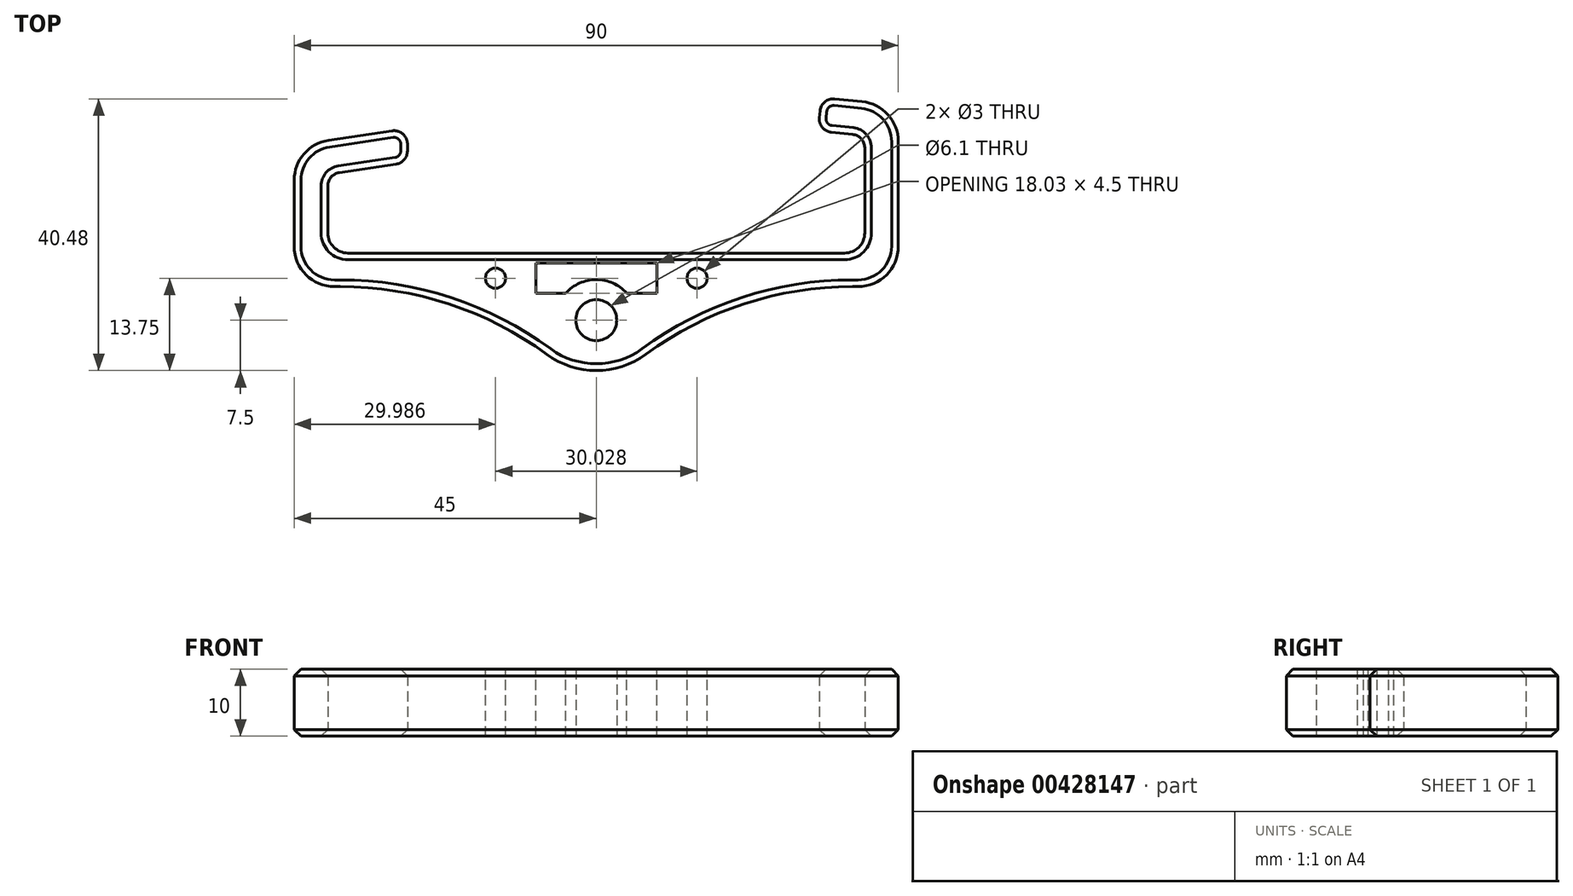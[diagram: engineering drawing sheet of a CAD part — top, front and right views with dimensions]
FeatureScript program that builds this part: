
annotation { "Feature Type Name" : "Feature", "Feature Type Description" : "" }
export const myFeature = defineFeature(function(context is Context, id is Id, definition is map)
    precondition{}
    {
        {
            var Q0;
            Q0=qCreatedBy(makeId("Right.planeOp"),FACE);
            var sketch = newSketch(context, id + "F0", { "sketchPlane" : qUnion([Q0])});
            skLineSegment(sketch, "E0", {"start": v(0, 77) * mm, "end": v(0, 3) * mm});
            skLineSegment(sketch, "E1", {"start": v(3, 80) * mm, "end": v(10, 80) * mm});
            skLineSegment(sketch, "E2", {"start": v(3, 0) * mm, "end": v(15.7, 0) * mm});
            skLineSegment(sketch, "E3", {"start": v(11.98, 78.3) * mm, "end": v(13.24, 69.84) * mm});
            skLineSegment(sketch, "E4", {"start": v(17.68, 1.8) * mm, "end": v(18, 4.97) * mm});
            skLineSegment(sketch, "E5.0", {"start": v(16.8, 79.89) * mm, "end": v(18.21, 70.43) * mm});
            skLineSegment(sketch, "E5.1", {"start": v(22.57, 0.4) * mm, "end": v(22.97, 4.47) * mm});
            skLineSegment(sketch, "E5.2", {"start": v(1, -5) * mm, "end": v(16.6, -5) * mm});
            skLineSegment(sketch, "E5.3", {"start": v(-5, 79) * mm, "end": v(-5, 78.16) * mm});
            skLineSegment(sketch, "E5.4", {"start": v(1, 85) * mm, "end": v(10.86, 85) * mm});
            skLineSegment(sketch, "E6", {"start": v(15.22, 68.13) * mm, "end": v(16.23, 68.13) * mm});
            skLineSegment(sketch, "E7", {"start": v(20.19, 6.76) * mm, "end": v(21.18, 6.66) * mm});
            skPoint(sketch, "E8.visualSharp", {"position": v(0, 72) * mm});
            skArc(sketch, "E8.filletArc", {"start": v(3, 80) * mm, "mid": v(0.88, 79.12) * mm, "end": v(0, 77) * mm});
            skPoint(sketch, "E9.visualSharp", {"position": v(11.72, 80) * mm});
            skArc(sketch, "E9.filletArc", {"start": v(11.98, 78.3) * mm, "mid": v(11.3, 79.52) * mm, "end": v(10, 80) * mm});
            skPoint(sketch, "E10.visualSharp", {"position": v(0, 0) * mm});
            skArc(sketch, "E10.filletArc", {"start": v(0, 3) * mm, "mid": v(0.88, 0.88) * mm, "end": v(3, 0) * mm});
            skPoint(sketch, "E11.visualSharp", {"position": v(17.5, 0) * mm});
            skArc(sketch, "E11.filletArc", {"start": v(15.7, 0) * mm, "mid": v(17.03, 0.52) * mm, "end": v(17.68, 1.8) * mm});
            skPoint(sketch, "E12.visualSharp", {"position": v(18.2, 6.96) * mm});
            skArc(sketch, "E12.filletArc", {"start": v(20.19, 6.76) * mm, "mid": v(18.72, 6.32) * mm, "end": v(18, 4.97) * mm});
            skPoint(sketch, "E13.visualSharp", {"position": v(23.17, 6.46) * mm});
            skArc(sketch, "E13.filletArc", {"start": v(22.97, 4.47) * mm, "mid": v(22.53, 5.94) * mm, "end": v(21.18, 6.66) * mm});
            skPoint(sketch, "E14.visualSharp", {"position": v(13.5, 68.13) * mm});
            skArc(sketch, "E14.filletArc", {"start": v(13.24, 69.84) * mm, "mid": v(13.92, 68.62) * mm, "end": v(15.22, 68.13) * mm});
            skPoint(sketch, "E15.visualSharp", {"position": v(18.56, 68.13) * mm});
            skArc(sketch, "E15.filletArc", {"start": v(16.23, 68.13) * mm, "mid": v(17.75, 68.83) * mm, "end": v(18.21, 70.43) * mm});
            skPoint(sketch, "E16.visualSharp", {"position": v(16.03, 85) * mm});
            skArc(sketch, "E16.filletArc", {"start": v(16.8, 79.89) * mm, "mid": v(14.78, 83.55) * mm, "end": v(10.86, 85) * mm});
            skPoint(sketch, "E17.visualSharp", {"position": v(-5, 85) * mm});
            skArc(sketch, "E17.filletArc", {"start": v(1, 85) * mm, "mid": v(-3.24, 83.24) * mm, "end": v(-5, 79) * mm});
            skPoint(sketch, "E18.visualSharp", {"position": v(22.02, -5) * mm});
            skArc(sketch, "E18.filletArc", {"start": v(16.6, -5) * mm, "mid": v(20.62, -3.45) * mm, "end": v(22.57, 0.4) * mm});
            skPoint(sketch, "E19.visualSharp", {"position": v(-5, -5) * mm});
            skArc(sketch, "E19.filletArc", {"start": v(-5, 1) * mm, "mid": v(-3.24, -3.24) * mm, "end": v(1, -5) * mm});
            skArc(sketch, "E20", {"start": v(-15.08, 47.4) * mm, "mid": v(-17.5, 40) * mm, "end": v(-15.08, 32.6) * mm});
            skLineSegment(sketch, "E21.trimOffspring", {"start": v(-5, 1.84) * mm, "end": v(-5, 1) * mm});
            skPoint(sketch, "E22.visualSharp", {"position": v(-5, 52.5) * mm});
            skArc(sketch, "E22.filletArc", {"start": v(-15.08, 47.4) * mm, "mid": v(-7.58, 61.97) * mm, "end": v(-5, 78.16) * mm});
            skPoint(sketch, "E23.visualSharp", {"position": v(-5, 27.5) * mm});
            skArc(sketch, "E23.filletArc", {"start": v(-5, 1.84) * mm, "mid": v(-7.58, 18.03) * mm, "end": v(-15.08, 32.6) * mm});
            skCircle(sketch, "E24", {"center": v(-10, 40) * mm, "radius": 3.05 * mm});
            skSolve(sketch);
        }
        {
            var Q0;
            Q0=makeQuery(id+"F0.imprint","IMPRINT",FACE,{"disambiguationData":[TD([[makeQuery(id+"F0.imprint","IMPRINT",EDGE,{"derivedFrom":sQuery(id+"F0.wireOp",EDGE,"E0")}),-1.0]])]});
            extrude(context, id + "F1", {"entities" : qUnion([Q0]), "depth" : 10 * mm});
        }
        {
            var Q0;
            Q0=makeQuery(id+"F1.opExtrude","SWEPT_BODY",BODY,{"disambiguationData":[OSD([sQuery(id+"F0.wireOp",EDGE,"E0"),sQuery(id+"F0.wireOp",EDGE,"E1"),sQuery(id+"F0.wireOp",EDGE,"E2"),sQuery(id+"F0.wireOp",EDGE,"E3"),sQuery(id+"F0.wireOp",EDGE,"E4"),sQuery(id+"F0.wireOp",EDGE,"E5.0"),sQuery(id+"F0.wireOp",EDGE,"E5.1"),sQuery(id+"F0.wireOp",EDGE,"E5.2"),sQuery(id+"F0.wireOp",EDGE,"E5.3"),sQuery(id+"F0.wireOp",EDGE,"E5.4"),sQuery(id+"F0.wireOp",EDGE,"E6"),sQuery(id+"F0.wireOp",EDGE,"E7"),sQuery(id+"F0.wireOp",EDGE,"E8.filletArc"),sQuery(id+"F0.wireOp",EDGE,"E9.filletArc"),sQuery(id+"F0.wireOp",EDGE,"E10.filletArc"),sQuery(id+"F0.wireOp",EDGE,"E11.filletArc"),sQuery(id+"F0.wireOp",EDGE,"E12.filletArc"),sQuery(id+"F0.wireOp",EDGE,"E13.filletArc"),sQuery(id+"F0.wireOp",EDGE,"E14.filletArc"),sQuery(id+"F0.wireOp",EDGE,"E15.filletArc"),sQuery(id+"F0.wireOp",EDGE,"E16.filletArc"),sQuery(id+"F0.wireOp",EDGE,"E17.filletArc"),sQuery(id+"F0.wireOp",EDGE,"E18.filletArc"),sQuery(id+"F0.wireOp",EDGE,"E19.filletArc"),sQuery(id+"F0.wireOp",EDGE,"E20"),sQuery(id+"F0.wireOp",EDGE,"E21.trimOffspring"),sQuery(id+"F0.wireOp",EDGE,"E22.filletArc"),sQuery(id+"F0.wireOp",EDGE,"E23.filletArc"),sQuery(id+"F0.wireOp",EDGE,"E24")])]});
            var Q1;
            Q1=makeQuery(id+"F1.opExtrude","CAP_EDGE",EDGE,{"disambiguationData":[OSD([sQuery(id+"F0.wireOp",EDGE,"E5.2")])],"isStart":true});
            transform(context, id + "F2", {"entities" : qUnion([Q0]), "transformType" : TransformType.ROTATION, "transformAxis" : qUnion([Q1]), "angle" : 90 * degree, "oppositeDirection" : true, "makeCopy" : false});
        }
        {
            var Q0;
            Q0=makeQuery(id+"F1.opExtrude","SWEPT_BODY",BODY,{"disambiguationData":[OSD([sQuery(id+"F0.wireOp",EDGE,"E0"),sQuery(id+"F0.wireOp",EDGE,"E1"),sQuery(id+"F0.wireOp",EDGE,"E2"),sQuery(id+"F0.wireOp",EDGE,"E3"),sQuery(id+"F0.wireOp",EDGE,"E4"),sQuery(id+"F0.wireOp",EDGE,"E5.0"),sQuery(id+"F0.wireOp",EDGE,"E5.1"),sQuery(id+"F0.wireOp",EDGE,"E5.2"),sQuery(id+"F0.wireOp",EDGE,"E5.3"),sQuery(id+"F0.wireOp",EDGE,"E5.4"),sQuery(id+"F0.wireOp",EDGE,"E6"),sQuery(id+"F0.wireOp",EDGE,"E7"),sQuery(id+"F0.wireOp",EDGE,"E8.filletArc"),sQuery(id+"F0.wireOp",EDGE,"E9.filletArc"),sQuery(id+"F0.wireOp",EDGE,"E10.filletArc"),sQuery(id+"F0.wireOp",EDGE,"E11.filletArc"),sQuery(id+"F0.wireOp",EDGE,"E12.filletArc"),sQuery(id+"F0.wireOp",EDGE,"E13.filletArc"),sQuery(id+"F0.wireOp",EDGE,"E14.filletArc"),sQuery(id+"F0.wireOp",EDGE,"E15.filletArc"),sQuery(id+"F0.wireOp",EDGE,"E16.filletArc"),sQuery(id+"F0.wireOp",EDGE,"E17.filletArc"),sQuery(id+"F0.wireOp",EDGE,"E18.filletArc"),sQuery(id+"F0.wireOp",EDGE,"E19.filletArc"),sQuery(id+"F0.wireOp",EDGE,"E20"),sQuery(id+"F0.wireOp",EDGE,"E21.trimOffspring"),sQuery(id+"F0.wireOp",EDGE,"E22.filletArc"),sQuery(id+"F0.wireOp",EDGE,"E23.filletArc"),sQuery(id+"F0.wireOp",EDGE,"E24")])]});
            transform(context, id + "F3", {"entities" : qUnion([Q0]), "transformType" : TransformType.TRANSLATION_3D, "dx" : 0 * mm, "dy" : 0 * mm, "dz" : 10 * mm, "makeCopy" : false});
        }
        {
            var Q0;
            Q0=makeQuery(id+"F1.opExtrude","SWEPT_BODY",BODY,{"disambiguationData":[OSD([sQuery(id+"F0.wireOp",EDGE,"E0"),sQuery(id+"F0.wireOp",EDGE,"E1"),sQuery(id+"F0.wireOp",EDGE,"E2"),sQuery(id+"F0.wireOp",EDGE,"E3"),sQuery(id+"F0.wireOp",EDGE,"E4"),sQuery(id+"F0.wireOp",EDGE,"E5.0"),sQuery(id+"F0.wireOp",EDGE,"E5.1"),sQuery(id+"F0.wireOp",EDGE,"E5.2"),sQuery(id+"F0.wireOp",EDGE,"E5.3"),sQuery(id+"F0.wireOp",EDGE,"E5.4"),sQuery(id+"F0.wireOp",EDGE,"E6"),sQuery(id+"F0.wireOp",EDGE,"E7"),sQuery(id+"F0.wireOp",EDGE,"E8.filletArc"),sQuery(id+"F0.wireOp",EDGE,"E9.filletArc"),sQuery(id+"F0.wireOp",EDGE,"E10.filletArc"),sQuery(id+"F0.wireOp",EDGE,"E11.filletArc"),sQuery(id+"F0.wireOp",EDGE,"E12.filletArc"),sQuery(id+"F0.wireOp",EDGE,"E13.filletArc"),sQuery(id+"F0.wireOp",EDGE,"E14.filletArc"),sQuery(id+"F0.wireOp",EDGE,"E15.filletArc"),sQuery(id+"F0.wireOp",EDGE,"E16.filletArc"),sQuery(id+"F0.wireOp",EDGE,"E17.filletArc"),sQuery(id+"F0.wireOp",EDGE,"E18.filletArc"),sQuery(id+"F0.wireOp",EDGE,"E19.filletArc"),sQuery(id+"F0.wireOp",EDGE,"E20"),sQuery(id+"F0.wireOp",EDGE,"E21.trimOffspring"),sQuery(id+"F0.wireOp",EDGE,"E22.filletArc"),sQuery(id+"F0.wireOp",EDGE,"E23.filletArc"),sQuery(id+"F0.wireOp",EDGE,"E24")])]});
            transform(context, id + "F4", {"entities" : qUnion([Q0]), "transformType" : TransformType.TRANSLATION_3D, "dx" : 0 * mm, "dy" : 0 * mm, "dz" : -10 * mm, "makeCopy" : false});
        }
        {
            var Q0;
            Q0=makeQuery(id+"F1.opExtrude","SWEPT_BODY",BODY,{"disambiguationData":[OSD([sQuery(id+"F0.wireOp",EDGE,"E0"),sQuery(id+"F0.wireOp",EDGE,"E1"),sQuery(id+"F0.wireOp",EDGE,"E2"),sQuery(id+"F0.wireOp",EDGE,"E3"),sQuery(id+"F0.wireOp",EDGE,"E4"),sQuery(id+"F0.wireOp",EDGE,"E5.0"),sQuery(id+"F0.wireOp",EDGE,"E5.1"),sQuery(id+"F0.wireOp",EDGE,"E5.2"),sQuery(id+"F0.wireOp",EDGE,"E5.3"),sQuery(id+"F0.wireOp",EDGE,"E5.4"),sQuery(id+"F0.wireOp",EDGE,"E6"),sQuery(id+"F0.wireOp",EDGE,"E7"),sQuery(id+"F0.wireOp",EDGE,"E8.filletArc"),sQuery(id+"F0.wireOp",EDGE,"E9.filletArc"),sQuery(id+"F0.wireOp",EDGE,"E10.filletArc"),sQuery(id+"F0.wireOp",EDGE,"E11.filletArc"),sQuery(id+"F0.wireOp",EDGE,"E12.filletArc"),sQuery(id+"F0.wireOp",EDGE,"E13.filletArc"),sQuery(id+"F0.wireOp",EDGE,"E14.filletArc"),sQuery(id+"F0.wireOp",EDGE,"E15.filletArc"),sQuery(id+"F0.wireOp",EDGE,"E16.filletArc"),sQuery(id+"F0.wireOp",EDGE,"E17.filletArc"),sQuery(id+"F0.wireOp",EDGE,"E18.filletArc"),sQuery(id+"F0.wireOp",EDGE,"E19.filletArc"),sQuery(id+"F0.wireOp",EDGE,"E20"),sQuery(id+"F0.wireOp",EDGE,"E21.trimOffspring"),sQuery(id+"F0.wireOp",EDGE,"E22.filletArc"),sQuery(id+"F0.wireOp",EDGE,"E23.filletArc"),sQuery(id+"F0.wireOp",EDGE,"E24")])]});
            transform(context, id + "F5", {"entities" : qUnion([Q0]), "transformType" : TransformType.TRANSLATION_3D, "dx" : 0 * mm, "dy" : 0 * mm, "dz" : 5 * mm, "makeCopy" : false});
        }
        {
            var Q0;
            Q0=makeQuery(id+"F1.opExtrude","SWEPT_BODY",BODY,{"disambiguationData":[OSD([sQuery(id+"F0.wireOp",EDGE,"E0"),sQuery(id+"F0.wireOp",EDGE,"E1"),sQuery(id+"F0.wireOp",EDGE,"E2"),sQuery(id+"F0.wireOp",EDGE,"E3"),sQuery(id+"F0.wireOp",EDGE,"E4"),sQuery(id+"F0.wireOp",EDGE,"E5.0"),sQuery(id+"F0.wireOp",EDGE,"E5.1"),sQuery(id+"F0.wireOp",EDGE,"E5.2"),sQuery(id+"F0.wireOp",EDGE,"E5.3"),sQuery(id+"F0.wireOp",EDGE,"E5.4"),sQuery(id+"F0.wireOp",EDGE,"E6"),sQuery(id+"F0.wireOp",EDGE,"E7"),sQuery(id+"F0.wireOp",EDGE,"E8.filletArc"),sQuery(id+"F0.wireOp",EDGE,"E9.filletArc"),sQuery(id+"F0.wireOp",EDGE,"E10.filletArc"),sQuery(id+"F0.wireOp",EDGE,"E11.filletArc"),sQuery(id+"F0.wireOp",EDGE,"E12.filletArc"),sQuery(id+"F0.wireOp",EDGE,"E13.filletArc"),sQuery(id+"F0.wireOp",EDGE,"E14.filletArc"),sQuery(id+"F0.wireOp",EDGE,"E15.filletArc"),sQuery(id+"F0.wireOp",EDGE,"E16.filletArc"),sQuery(id+"F0.wireOp",EDGE,"E17.filletArc"),sQuery(id+"F0.wireOp",EDGE,"E18.filletArc"),sQuery(id+"F0.wireOp",EDGE,"E19.filletArc"),sQuery(id+"F0.wireOp",EDGE,"E20"),sQuery(id+"F0.wireOp",EDGE,"E21.trimOffspring"),sQuery(id+"F0.wireOp",EDGE,"E22.filletArc"),sQuery(id+"F0.wireOp",EDGE,"E23.filletArc"),sQuery(id+"F0.wireOp",EDGE,"E24")])]});
            transform(context, id + "F6", {"entities" : qUnion([Q0]), "transformType" : TransformType.TRANSLATION_3D, "dx" : 40 * mm, "dy" : 0 * mm, "dz" : 0 * mm, "makeCopy" : false});
        }
        {
            var Q0;
            Q0=makeQuery(id+"F1.opExtrude","CAP_FACE",FACE,{"disambiguationData":[OSD([sQuery(id+"F0.wireOp",EDGE,"E0"),sQuery(id+"F0.wireOp",EDGE,"E1"),sQuery(id+"F0.wireOp",EDGE,"E2"),sQuery(id+"F0.wireOp",EDGE,"E3"),sQuery(id+"F0.wireOp",EDGE,"E4"),sQuery(id+"F0.wireOp",EDGE,"E5.0"),sQuery(id+"F0.wireOp",EDGE,"E5.1"),sQuery(id+"F0.wireOp",EDGE,"E5.2"),sQuery(id+"F0.wireOp",EDGE,"E5.3"),sQuery(id+"F0.wireOp",EDGE,"E5.4"),sQuery(id+"F0.wireOp",EDGE,"E6"),sQuery(id+"F0.wireOp",EDGE,"E7"),sQuery(id+"F0.wireOp",EDGE,"E8.filletArc"),sQuery(id+"F0.wireOp",EDGE,"E9.filletArc"),sQuery(id+"F0.wireOp",EDGE,"E10.filletArc"),sQuery(id+"F0.wireOp",EDGE,"E11.filletArc"),sQuery(id+"F0.wireOp",EDGE,"E12.filletArc"),sQuery(id+"F0.wireOp",EDGE,"E13.filletArc"),sQuery(id+"F0.wireOp",EDGE,"E14.filletArc"),sQuery(id+"F0.wireOp",EDGE,"E15.filletArc"),sQuery(id+"F0.wireOp",EDGE,"E16.filletArc"),sQuery(id+"F0.wireOp",EDGE,"E17.filletArc"),sQuery(id+"F0.wireOp",EDGE,"E18.filletArc"),sQuery(id+"F0.wireOp",EDGE,"E19.filletArc"),sQuery(id+"F0.wireOp",EDGE,"E20"),sQuery(id+"F0.wireOp",EDGE,"E21.trimOffspring"),sQuery(id+"F0.wireOp",EDGE,"E22.filletArc"),sQuery(id+"F0.wireOp",EDGE,"E23.filletArc"),sQuery(id+"F0.wireOp",EDGE,"E24")])],"isStart":false});
            var sketch = newSketch(context, id + "F7", { "sketchPlane" : qUnion([Q0])});
            skLineSegment(sketch, "E25", {"start": v(-5, -10) * mm, "end": v(-5, 3.8) * mm, "construction": true});
            skPoint(sketch, "E25.endSnap0", {"position": v(-5, 0) * mm});
            skLineSegment(sketch, "E26", {"start": v(4.01, -1.5) * mm, "end": v(4.01, -6) * mm});
            skLineSegment(sketch, "E27", {"start": v(4.01, -6) * mm, "end": v(-0.46, -6) * mm});
            skLineSegment(sketch, "E28", {"start": v(-14.01, -6) * mm, "end": v(-14.01, -1.5) * mm});
            skLineSegment(sketch, "E29", {"start": v(-14.01, -1.5) * mm, "end": v(4.01, -1.5) * mm});
            skArc(sketch, "E30", {"start": v(-0.46, -6) * mm, "mid": v(-5, -3.95) * mm, "end": v(-9.54, -6) * mm});
            skLineSegment(sketch, "E31.trimOffspring", {"start": v(-9.54, -6) * mm, "end": v(-14.01, -6) * mm});
            skLineSegment(sketch, "E32", {"start": v(-14.01, -3.75) * mm, "end": v(19.58, -3.75) * mm, "construction": true});
            skLineSegment(sketch, "E33", {"start": v(-14.01, -3.75) * mm, "end": v(-26.01, -3.75) * mm, "construction": true});
            skCircle(sketch, "E34", {"center": v(-20.01, -3.75) * mm, "radius": 1.5 * mm});
            skCircle(sketch, "E35", {"center": v(10.01, -3.75) * mm, "radius": 1.5 * mm});
            skSolve(sketch);
        }
        {
            var Q0;
            Q0=makeQuery(id+"F7.imprint","IMPRINT",FACE,{"disambiguationData":[TD([[makeQuery(id+"F7.imprint","IMPRINT",EDGE,{"derivedFrom":sQuery(id+"F7.wireOp",EDGE,"E26")}),-1.0]])]});
            var Q1;
            Q1=makeQuery(id+"F7.imprint","IMPRINT",FACE,{"disambiguationData":[TD([[makeQuery(id+"F7.imprint","IMPRINT",EDGE,{"derivedFrom":sQuery(id+"F7.wireOp",EDGE,"E34")}),1.0]])]});
            var Q2;
            Q2=makeQuery(id+"F7.imprint","IMPRINT",FACE,{"disambiguationData":[TD([[makeQuery(id+"F7.imprint","IMPRINT",EDGE,{"derivedFrom":sQuery(id+"F7.wireOp",EDGE,"E35")}),1.0]])]});
            extrude(context, id + "F8", {"entities" : qUnion([Q0, Q1, Q2]), "operationType" : NewBodyOperationType.REMOVE, "endBound" : BoundingType.UP_TO_NEXT, "oppositeDirection" : true, "depth" : 25 * mm});
        }
        {
            var Q0;
            Q0=makeQuery(id+"F1.opExtrude","CAP_EDGE",EDGE,{"disambiguationData":[OSD([sQuery(id+"F0.wireOp",EDGE,"E0")])],"isStart":false});
            var Q1;
            Q1=makeQuery(id+"F1.opExtrude","CAP_EDGE",EDGE,{"disambiguationData":[OSD([sQuery(id+"F0.wireOp",EDGE,"E8.filletArc")])],"isStart":false});
            var Q2;
            Q2=makeQuery(id+"F1.opExtrude","CAP_EDGE",EDGE,{"disambiguationData":[OSD([sQuery(id+"F0.wireOp",EDGE,"E1")])],"isStart":false});
            var Q3;
            Q3=makeQuery(id+"F1.opExtrude","CAP_EDGE",EDGE,{"disambiguationData":[OSD([sQuery(id+"F0.wireOp",EDGE,"E9.filletArc")])],"isStart":false});
            var Q4;
            Q4=makeQuery(id+"F1.opExtrude","CAP_EDGE",EDGE,{"disambiguationData":[OSD([sQuery(id+"F0.wireOp",EDGE,"E3")])],"isStart":false});
            var Q5;
            Q5=makeQuery(id+"F1.opExtrude","CAP_EDGE",EDGE,{"disambiguationData":[OSD([sQuery(id+"F0.wireOp",EDGE,"E14.filletArc")])],"isStart":false});
            var Q6;
            Q6=makeQuery(id+"F1.opExtrude","CAP_EDGE",EDGE,{"disambiguationData":[OSD([sQuery(id+"F0.wireOp",EDGE,"E6")])],"isStart":false});
            var Q7;
            Q7=makeQuery(id+"F1.opExtrude","CAP_EDGE",EDGE,{"disambiguationData":[OSD([sQuery(id+"F0.wireOp",EDGE,"E15.filletArc")])],"isStart":false});
            var Q8;
            Q8=makeQuery(id+"F1.opExtrude","CAP_EDGE",EDGE,{"disambiguationData":[OSD([sQuery(id+"F0.wireOp",EDGE,"E5.0")])],"isStart":false});
            var Q9;
            Q9=makeQuery(id+"F1.opExtrude","CAP_EDGE",EDGE,{"disambiguationData":[OSD([sQuery(id+"F0.wireOp",EDGE,"E16.filletArc")])],"isStart":false});
            var Q10;
            Q10=makeQuery(id+"F1.opExtrude","CAP_EDGE",EDGE,{"disambiguationData":[OSD([sQuery(id+"F0.wireOp",EDGE,"E5.4")])],"isStart":false});
            var Q11;
            Q11=makeQuery(id+"F1.opExtrude","CAP_EDGE",EDGE,{"disambiguationData":[OSD([sQuery(id+"F0.wireOp",EDGE,"E17.filletArc")])],"isStart":false});
            var Q12;
            Q12=makeQuery(id+"F1.opExtrude","CAP_EDGE",EDGE,{"disambiguationData":[OSD([sQuery(id+"F0.wireOp",EDGE,"E5.3")])],"isStart":false});
            var Q13;
            Q13=makeQuery(id+"F1.opExtrude","CAP_EDGE",EDGE,{"disambiguationData":[OSD([sQuery(id+"F0.wireOp",EDGE,"E22.filletArc")])],"isStart":false});
            var Q14;
            Q14=makeQuery(id+"F1.opExtrude","CAP_EDGE",EDGE,{"disambiguationData":[OSD([sQuery(id+"F0.wireOp",EDGE,"E20")])],"isStart":false});
            var Q15;
            Q15=makeQuery(id+"F1.opExtrude","CAP_EDGE",EDGE,{"disambiguationData":[OSD([sQuery(id+"F0.wireOp",EDGE,"E23.filletArc")])],"isStart":false});
            var Q16;
            Q16=makeQuery(id+"F1.opExtrude","CAP_EDGE",EDGE,{"disambiguationData":[OSD([sQuery(id+"F0.wireOp",EDGE,"E21.trimOffspring")])],"isStart":false});
            var Q17;
            Q17=makeQuery(id+"F1.opExtrude","CAP_EDGE",EDGE,{"disambiguationData":[OSD([sQuery(id+"F0.wireOp",EDGE,"E19.filletArc")])],"isStart":false});
            var Q18;
            Q18=makeQuery(id+"F1.opExtrude","CAP_EDGE",EDGE,{"disambiguationData":[OSD([sQuery(id+"F0.wireOp",EDGE,"E5.2")])],"isStart":false});
            var Q19;
            Q19=makeQuery(id+"F1.opExtrude","CAP_EDGE",EDGE,{"disambiguationData":[OSD([sQuery(id+"F0.wireOp",EDGE,"E18.filletArc")])],"isStart":false});
            var Q20;
            Q20=makeQuery(id+"F1.opExtrude","CAP_EDGE",EDGE,{"disambiguationData":[OSD([sQuery(id+"F0.wireOp",EDGE,"E5.1")])],"isStart":false});
            var Q21;
            Q21=makeQuery(id+"F1.opExtrude","CAP_EDGE",EDGE,{"disambiguationData":[OSD([sQuery(id+"F0.wireOp",EDGE,"E13.filletArc")])],"isStart":false});
            var Q22;
            Q22=makeQuery(id+"F1.opExtrude","CAP_EDGE",EDGE,{"disambiguationData":[OSD([sQuery(id+"F0.wireOp",EDGE,"E7")])],"isStart":false});
            var Q23;
            Q23=makeQuery(id+"F1.opExtrude","CAP_EDGE",EDGE,{"disambiguationData":[OSD([sQuery(id+"F0.wireOp",EDGE,"E12.filletArc")])],"isStart":false});
            var Q24;
            Q24=makeQuery(id+"F1.opExtrude","CAP_EDGE",EDGE,{"disambiguationData":[OSD([sQuery(id+"F0.wireOp",EDGE,"E4")])],"isStart":false});
            var Q25;
            Q25=makeQuery(id+"F1.opExtrude","CAP_EDGE",EDGE,{"disambiguationData":[OSD([sQuery(id+"F0.wireOp",EDGE,"E11.filletArc")])],"isStart":false});
            var Q26;
            Q26=makeQuery(id+"F1.opExtrude","CAP_EDGE",EDGE,{"disambiguationData":[OSD([sQuery(id+"F0.wireOp",EDGE,"E2")])],"isStart":false});
            var Q27;
            Q27=makeQuery(id+"F1.opExtrude","CAP_EDGE",EDGE,{"disambiguationData":[OSD([sQuery(id+"F0.wireOp",EDGE,"E10.filletArc")])],"isStart":false});
            chamfer(context, id + "F9", {"entities" : qUnion([Q0, Q1, Q2, Q3, Q4, Q5, Q6, Q7, Q8, Q9, Q10, Q11, Q12, Q13, Q14, Q15, Q16, Q17, Q18, Q19, Q20, Q21, Q22, Q23, Q24, Q25, Q26, Q27]), "width" : 1 * mm, "tangentPropagation" : true});
        }
        {
            var Q0;
            Q0=makeQuery(id+"F1.opExtrude","CAP_EDGE",EDGE,{"disambiguationData":[OSD([sQuery(id+"F0.wireOp",EDGE,"E0")])],"isStart":true});
            var Q1;
            Q1=makeQuery(id+"F1.opExtrude","CAP_EDGE",EDGE,{"disambiguationData":[OSD([sQuery(id+"F0.wireOp",EDGE,"E10.filletArc")])],"isStart":true});
            var Q2;
            Q2=makeQuery(id+"F1.opExtrude","CAP_EDGE",EDGE,{"disambiguationData":[OSD([sQuery(id+"F0.wireOp",EDGE,"E2")])],"isStart":true});
            var Q3;
            Q3=makeQuery(id+"F1.opExtrude","CAP_EDGE",EDGE,{"disambiguationData":[OSD([sQuery(id+"F0.wireOp",EDGE,"E11.filletArc")])],"isStart":true});
            var Q4;
            Q4=makeQuery(id+"F1.opExtrude","CAP_EDGE",EDGE,{"disambiguationData":[OSD([sQuery(id+"F0.wireOp",EDGE,"E4")])],"isStart":true});
            var Q5;
            Q5=makeQuery(id+"F1.opExtrude","CAP_EDGE",EDGE,{"disambiguationData":[OSD([sQuery(id+"F0.wireOp",EDGE,"E12.filletArc")])],"isStart":true});
            var Q6;
            Q6=makeQuery(id+"F1.opExtrude","CAP_EDGE",EDGE,{"disambiguationData":[OSD([sQuery(id+"F0.wireOp",EDGE,"E7")])],"isStart":true});
            var Q7;
            Q7=makeQuery(id+"F1.opExtrude","CAP_EDGE",EDGE,{"disambiguationData":[OSD([sQuery(id+"F0.wireOp",EDGE,"E13.filletArc")])],"isStart":true});
            var Q8;
            Q8=makeQuery(id+"F1.opExtrude","CAP_EDGE",EDGE,{"disambiguationData":[OSD([sQuery(id+"F0.wireOp",EDGE,"E5.1")])],"isStart":true});
            var Q9;
            Q9=makeQuery(id+"F1.opExtrude","CAP_EDGE",EDGE,{"disambiguationData":[OSD([sQuery(id+"F0.wireOp",EDGE,"E18.filletArc")])],"isStart":true});
            var Q10;
            Q10=makeQuery(id+"F1.opExtrude","CAP_EDGE",EDGE,{"disambiguationData":[OSD([sQuery(id+"F0.wireOp",EDGE,"E5.2")])],"isStart":true});
            var Q11;
            Q11=makeQuery(id+"F1.opExtrude","CAP_EDGE",EDGE,{"disambiguationData":[OSD([sQuery(id+"F0.wireOp",EDGE,"E19.filletArc")])],"isStart":true});
            var Q12;
            Q12=makeQuery(id+"F1.opExtrude","CAP_EDGE",EDGE,{"disambiguationData":[OSD([sQuery(id+"F0.wireOp",EDGE,"E21.trimOffspring")])],"isStart":true});
            var Q13;
            Q13=makeQuery(id+"F1.opExtrude","CAP_EDGE",EDGE,{"disambiguationData":[OSD([sQuery(id+"F0.wireOp",EDGE,"E23.filletArc")])],"isStart":true});
            var Q14;
            Q14=makeQuery(id+"F1.opExtrude","CAP_EDGE",EDGE,{"disambiguationData":[OSD([sQuery(id+"F0.wireOp",EDGE,"E20")])],"isStart":true});
            var Q15;
            Q15=makeQuery(id+"F1.opExtrude","CAP_EDGE",EDGE,{"disambiguationData":[OSD([sQuery(id+"F0.wireOp",EDGE,"E22.filletArc")])],"isStart":true});
            var Q16;
            Q16=makeQuery(id+"F1.opExtrude","CAP_EDGE",EDGE,{"disambiguationData":[OSD([sQuery(id+"F0.wireOp",EDGE,"E5.3")])],"isStart":true});
            var Q17;
            Q17=makeQuery(id+"F1.opExtrude","CAP_EDGE",EDGE,{"disambiguationData":[OSD([sQuery(id+"F0.wireOp",EDGE,"E17.filletArc")])],"isStart":true});
            var Q18;
            Q18=makeQuery(id+"F1.opExtrude","CAP_EDGE",EDGE,{"disambiguationData":[OSD([sQuery(id+"F0.wireOp",EDGE,"E5.4")])],"isStart":true});
            var Q19;
            Q19=makeQuery(id+"F1.opExtrude","CAP_EDGE",EDGE,{"disambiguationData":[OSD([sQuery(id+"F0.wireOp",EDGE,"E16.filletArc")])],"isStart":true});
            var Q20;
            Q20=makeQuery(id+"F1.opExtrude","CAP_EDGE",EDGE,{"disambiguationData":[OSD([sQuery(id+"F0.wireOp",EDGE,"E5.0")])],"isStart":true});
            var Q21;
            Q21=makeQuery(id+"F1.opExtrude","CAP_EDGE",EDGE,{"disambiguationData":[OSD([sQuery(id+"F0.wireOp",EDGE,"E15.filletArc")])],"isStart":true});
            var Q22;
            Q22=makeQuery(id+"F1.opExtrude","CAP_EDGE",EDGE,{"disambiguationData":[OSD([sQuery(id+"F0.wireOp",EDGE,"E6")])],"isStart":true});
            var Q23;
            Q23=makeQuery(id+"F1.opExtrude","CAP_EDGE",EDGE,{"disambiguationData":[OSD([sQuery(id+"F0.wireOp",EDGE,"E14.filletArc")])],"isStart":true});
            var Q24;
            Q24=makeQuery(id+"F1.opExtrude","CAP_EDGE",EDGE,{"disambiguationData":[OSD([sQuery(id+"F0.wireOp",EDGE,"E3")])],"isStart":true});
            var Q25;
            Q25=makeQuery(id+"F1.opExtrude","CAP_EDGE",EDGE,{"disambiguationData":[OSD([sQuery(id+"F0.wireOp",EDGE,"E9.filletArc")])],"isStart":true});
            var Q26;
            Q26=makeQuery(id+"F1.opExtrude","CAP_EDGE",EDGE,{"disambiguationData":[OSD([sQuery(id+"F0.wireOp",EDGE,"E1")])],"isStart":true});
            var Q27;
            Q27=makeQuery(id+"F1.opExtrude","CAP_EDGE",EDGE,{"disambiguationData":[OSD([sQuery(id+"F0.wireOp",EDGE,"E8.filletArc")])],"isStart":true});
            chamfer(context, id + "F10", {"entities" : qUnion([Q0, Q1, Q2, Q3, Q4, Q5, Q6, Q7, Q8, Q9, Q10, Q11, Q12, Q13, Q14, Q15, Q16, Q17, Q18, Q19, Q20, Q21, Q22, Q23, Q24, Q25, Q26, Q27]), "width" : 1 * mm, "tangentPropagation" : true});
        }
    });
